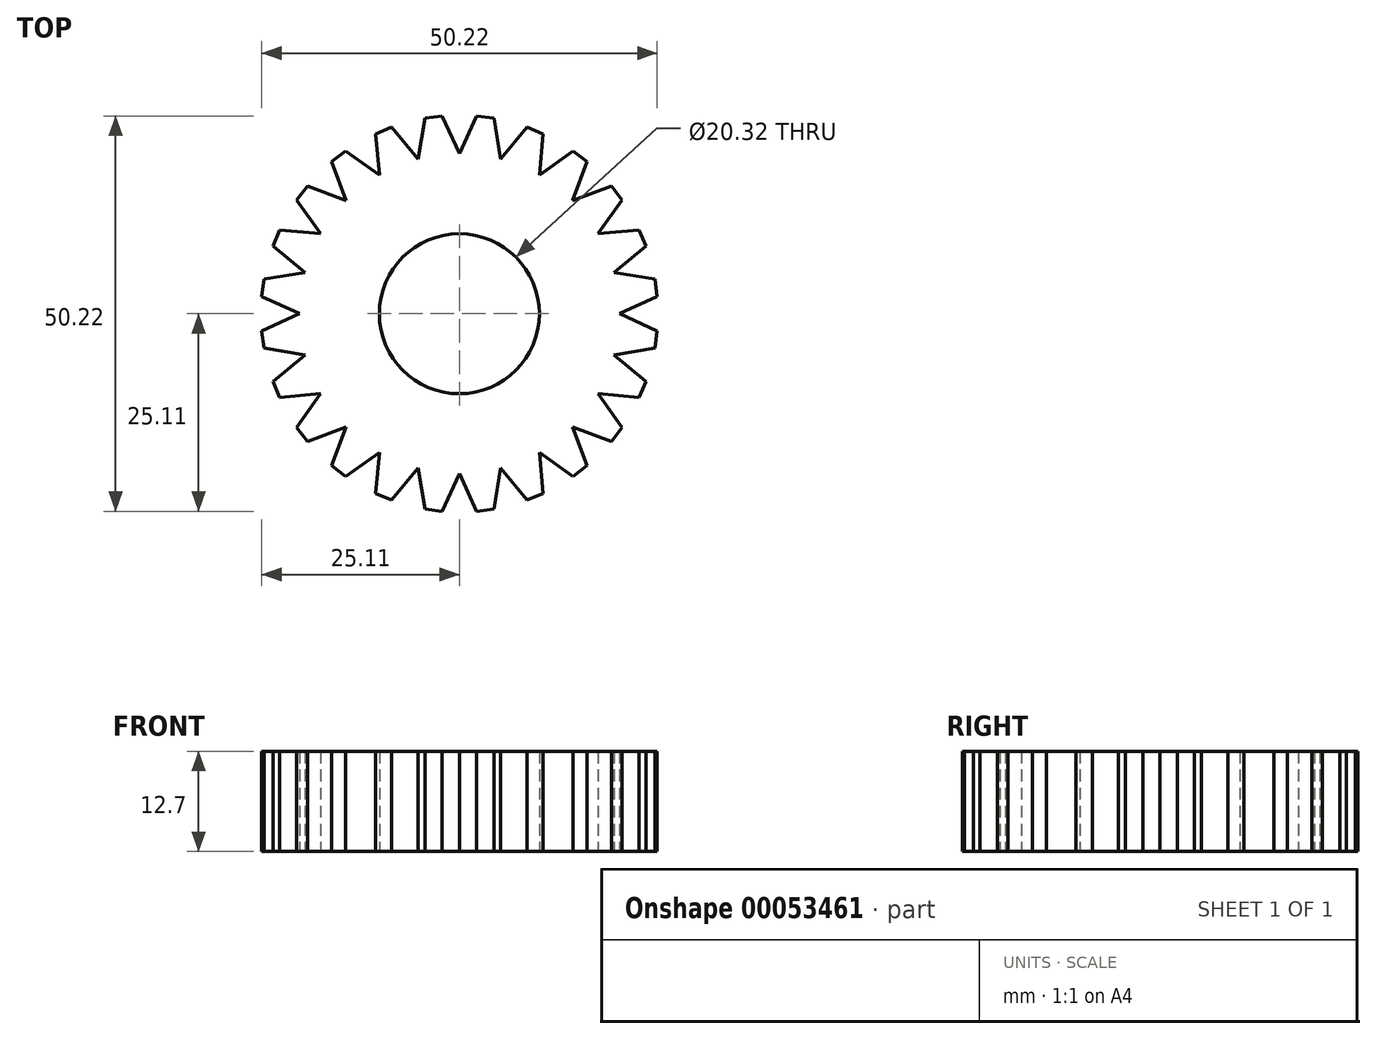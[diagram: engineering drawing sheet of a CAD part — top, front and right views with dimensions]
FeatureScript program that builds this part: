
annotation { "Feature Type Name" : "Feature", "Feature Type Description" : "" }
export const myFeature = defineFeature(function(context is Context, id is Id, definition is map)
    precondition{}
    {
        {
            var Q0;
            Q0=qCreatedBy(makeId("Top.planeOp"),FACE);
            var sketch = newSketch(context, id + "F0", { "sketchPlane" : qUnion([Q0])});
            skLineSegment(sketch, "E0", {"start": v(-4.38, 24.82) * mm, "end": v(-5.26, 19.63) * mm});
            skLineSegment(sketch, "E1", {"start": v(-4.38, 24.82) * mm, "end": v(-2.2, 25.11) * mm});
            skLineSegment(sketch, "E2", {"start": v(-2.2, 25.11) * mm, "end": v(0, 20.32) * mm});
            skLineSegment(sketch, "E3", {"start": v(-10.66, 22.84) * mm, "end": v(-10.16, 17.6) * mm});
            skLineSegment(sketch, "E4", {"start": v(-10.66, 22.84) * mm, "end": v(-8.62, 23.69) * mm});
            skLineSegment(sketch, "E5", {"start": v(-8.62, 23.69) * mm, "end": v(-5.26, 19.63) * mm});
            skLineSegment(sketch, "E6", {"start": v(-16.2, 19.3) * mm, "end": v(-14.37, 14.37) * mm});
            skLineSegment(sketch, "E7", {"start": v(-16.2, 19.3) * mm, "end": v(-14.45, 20.65) * mm});
            skLineSegment(sketch, "E8", {"start": v(-14.45, 20.65) * mm, "end": v(-10.16, 17.6) * mm});
            skLineSegment(sketch, "E9", {"start": v(-20.65, 14.45) * mm, "end": v(-17.6, 10.16) * mm});
            skLineSegment(sketch, "E10", {"start": v(-20.65, 14.45) * mm, "end": v(-19.3, 16.2) * mm});
            skLineSegment(sketch, "E11", {"start": v(-19.3, 16.2) * mm, "end": v(-14.37, 14.37) * mm});
            skLineSegment(sketch, "E12", {"start": v(-23.69, 8.62) * mm, "end": v(-19.63, 5.26) * mm});
            skLineSegment(sketch, "E13", {"start": v(-23.69, 8.62) * mm, "end": v(-22.84, 10.66) * mm});
            skLineSegment(sketch, "E14", {"start": v(-22.84, 10.66) * mm, "end": v(-17.6, 10.16) * mm});
            skLineSegment(sketch, "E15", {"start": v(-25.11, 2.2) * mm, "end": v(-20.32, 0) * mm});
            skLineSegment(sketch, "E16", {"start": v(-25.11, 2.2) * mm, "end": v(-24.82, 4.38) * mm});
            skLineSegment(sketch, "E17", {"start": v(-24.82, 4.38) * mm, "end": v(-19.63, 5.26) * mm});
            skLineSegment(sketch, "E18", {"start": v(-24.82, -4.38) * mm, "end": v(-19.63, -5.26) * mm});
            skLineSegment(sketch, "E19", {"start": v(-24.82, -4.38) * mm, "end": v(-25.11, -2.2) * mm});
            skLineSegment(sketch, "E20", {"start": v(-25.11, -2.2) * mm, "end": v(-20.32, 0) * mm});
            skLineSegment(sketch, "E21", {"start": v(-22.84, -10.66) * mm, "end": v(-17.6, -10.16) * mm});
            skLineSegment(sketch, "E22", {"start": v(-22.84, -10.66) * mm, "end": v(-23.69, -8.62) * mm});
            skLineSegment(sketch, "E23", {"start": v(-23.69, -8.62) * mm, "end": v(-19.63, -5.26) * mm});
            skLineSegment(sketch, "E24", {"start": v(-19.3, -16.2) * mm, "end": v(-14.37, -14.37) * mm});
            skLineSegment(sketch, "E25", {"start": v(-19.3, -16.2) * mm, "end": v(-20.65, -14.45) * mm});
            skLineSegment(sketch, "E26", {"start": v(-20.65, -14.45) * mm, "end": v(-17.6, -10.16) * mm});
            skLineSegment(sketch, "E27", {"start": v(-14.45, -20.65) * mm, "end": v(-10.16, -17.6) * mm});
            skLineSegment(sketch, "E28", {"start": v(-14.45, -20.65) * mm, "end": v(-16.2, -19.3) * mm});
            skLineSegment(sketch, "E29", {"start": v(-16.2, -19.3) * mm, "end": v(-14.37, -14.37) * mm});
            skLineSegment(sketch, "E30", {"start": v(-8.62, -23.69) * mm, "end": v(-5.26, -19.63) * mm});
            skLineSegment(sketch, "E31", {"start": v(-8.62, -23.69) * mm, "end": v(-10.66, -22.84) * mm});
            skLineSegment(sketch, "E32", {"start": v(-10.66, -22.84) * mm, "end": v(-10.16, -17.6) * mm});
            skLineSegment(sketch, "E33", {"start": v(-2.2, -25.11) * mm, "end": v(0, -20.32) * mm});
            skLineSegment(sketch, "E34", {"start": v(-2.2, -25.11) * mm, "end": v(-4.38, -24.82) * mm});
            skLineSegment(sketch, "E35", {"start": v(-4.38, -24.82) * mm, "end": v(-5.26, -19.63) * mm});
            skLineSegment(sketch, "E36", {"start": v(4.38, -24.82) * mm, "end": v(5.26, -19.63) * mm});
            skLineSegment(sketch, "E37", {"start": v(4.38, -24.82) * mm, "end": v(2.2, -25.11) * mm});
            skLineSegment(sketch, "E38", {"start": v(2.2, -25.11) * mm, "end": v(0, -20.32) * mm});
            skLineSegment(sketch, "E39", {"start": v(10.66, -22.84) * mm, "end": v(10.16, -17.6) * mm});
            skLineSegment(sketch, "E40", {"start": v(10.66, -22.84) * mm, "end": v(8.62, -23.69) * mm});
            skLineSegment(sketch, "E41", {"start": v(8.62, -23.69) * mm, "end": v(5.26, -19.63) * mm});
            skLineSegment(sketch, "E42", {"start": v(16.2, -19.3) * mm, "end": v(14.37, -14.37) * mm});
            skLineSegment(sketch, "E43", {"start": v(16.2, -19.3) * mm, "end": v(14.45, -20.65) * mm});
            skLineSegment(sketch, "E44", {"start": v(14.45, -20.65) * mm, "end": v(10.16, -17.6) * mm});
            skLineSegment(sketch, "E45", {"start": v(20.65, -14.45) * mm, "end": v(17.6, -10.16) * mm});
            skLineSegment(sketch, "E46", {"start": v(20.65, -14.45) * mm, "end": v(19.3, -16.2) * mm});
            skLineSegment(sketch, "E47", {"start": v(19.3, -16.2) * mm, "end": v(14.37, -14.37) * mm});
            skLineSegment(sketch, "E48", {"start": v(23.69, -8.62) * mm, "end": v(19.63, -5.26) * mm});
            skLineSegment(sketch, "E49", {"start": v(23.69, -8.62) * mm, "end": v(22.84, -10.66) * mm});
            skLineSegment(sketch, "E50", {"start": v(22.84, -10.66) * mm, "end": v(17.6, -10.16) * mm});
            skLineSegment(sketch, "E51", {"start": v(25.11, -2.2) * mm, "end": v(20.32, 0) * mm});
            skLineSegment(sketch, "E52", {"start": v(25.11, -2.2) * mm, "end": v(24.82, -4.38) * mm});
            skLineSegment(sketch, "E53", {"start": v(24.82, -4.38) * mm, "end": v(19.63, -5.26) * mm});
            skLineSegment(sketch, "E54", {"start": v(24.82, 4.38) * mm, "end": v(19.63, 5.26) * mm});
            skLineSegment(sketch, "E55", {"start": v(24.82, 4.38) * mm, "end": v(25.11, 2.2) * mm});
            skLineSegment(sketch, "E56", {"start": v(25.11, 2.2) * mm, "end": v(20.32, 0) * mm});
            skLineSegment(sketch, "E57", {"start": v(22.84, 10.66) * mm, "end": v(17.6, 10.16) * mm});
            skLineSegment(sketch, "E58", {"start": v(22.84, 10.66) * mm, "end": v(23.69, 8.62) * mm});
            skLineSegment(sketch, "E59", {"start": v(23.69, 8.62) * mm, "end": v(19.63, 5.26) * mm});
            skLineSegment(sketch, "E60", {"start": v(19.3, 16.2) * mm, "end": v(14.37, 14.37) * mm});
            skLineSegment(sketch, "E61", {"start": v(19.3, 16.2) * mm, "end": v(20.65, 14.45) * mm});
            skLineSegment(sketch, "E62", {"start": v(20.65, 14.45) * mm, "end": v(17.6, 10.16) * mm});
            skLineSegment(sketch, "E63", {"start": v(14.45, 20.65) * mm, "end": v(10.16, 17.6) * mm});
            skLineSegment(sketch, "E64", {"start": v(14.45, 20.65) * mm, "end": v(16.2, 19.3) * mm});
            skLineSegment(sketch, "E65", {"start": v(16.2, 19.3) * mm, "end": v(14.37, 14.37) * mm});
            skLineSegment(sketch, "E66", {"start": v(8.62, 23.69) * mm, "end": v(5.26, 19.63) * mm});
            skLineSegment(sketch, "E67", {"start": v(8.62, 23.69) * mm, "end": v(10.66, 22.84) * mm});
            skLineSegment(sketch, "E68", {"start": v(10.66, 22.84) * mm, "end": v(10.16, 17.6) * mm});
            skLineSegment(sketch, "E69", {"start": v(2.2, 25.11) * mm, "end": v(0, 20.32) * mm});
            skLineSegment(sketch, "E70", {"start": v(2.2, 25.11) * mm, "end": v(4.38, 24.82) * mm});
            skLineSegment(sketch, "E71", {"start": v(4.38, 24.82) * mm, "end": v(5.26, 19.63) * mm});
            skCircle(sketch, "E72", {"center": v(0, 0) * mm, "radius": 10.16 * mm});
            skCircle(sketch, "E73", {"center": v(0, 0) * mm, "radius": 3.81 * mm});
            skSolve(sketch);
        }
        {
            var Q0;
            Q0=makeQuery(id+"F0.imprint","IMPRINT",FACE,{"disambiguationData":[TD([[makeQuery(id+"F0.imprint","IMPRINT",EDGE,{"derivedFrom":sQuery(id+"F0.wireOp",EDGE,"E0")}),1.0]])]});
            extrude(context, id + "F1", {"entities" : qUnion([Q0]), "depth" : 9.14 * mm});
        }
        {
            var Q0;
            Q0=makeQuery(id+"F0.imprint","IMPRINT",FACE,{"disambiguationData":[TD([[makeQuery(id+"F0.imprint","IMPRINT",EDGE,{"derivedFrom":sQuery(id+"F0.wireOp",EDGE,"E72")}),-1.0]])]});
            extrude(context, id + "F2", {"entities" : qUnion([Q0]), "operationType" : NewBodyOperationType.ADD, "depth" : 10.92 * mm});
        }
        {
            var Q0;
            Q0=makeQuery(id+"F0.imprint","IMPRINT",FACE,{"disambiguationData":[TD([[makeQuery(id+"F0.imprint","IMPRINT",EDGE,{"derivedFrom":sQuery(id+"F0.wireOp",EDGE,"E72")}),-1.0]])]});
            extrude(context, id + "F3", {"entities" : qUnion([Q0]), "operationType" : NewBodyOperationType.ADD, "oppositeDirection" : true, "depth" : 1.78 * mm});
        }
    });
